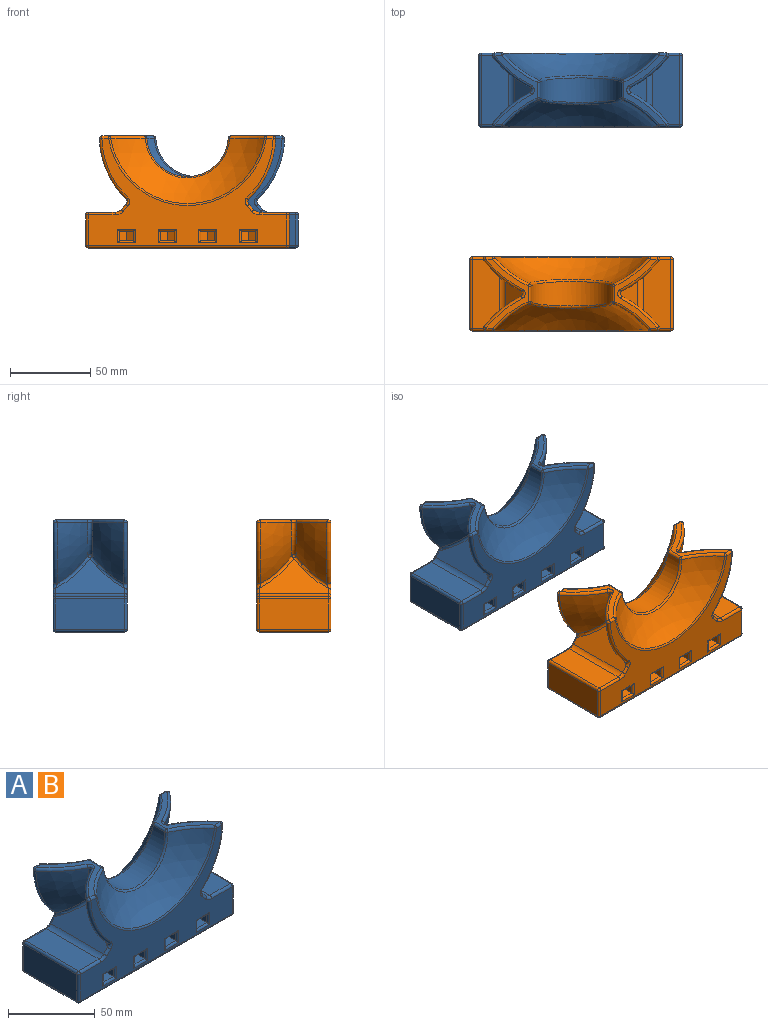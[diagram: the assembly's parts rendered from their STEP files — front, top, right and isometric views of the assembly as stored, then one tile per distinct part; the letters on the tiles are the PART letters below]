
ASSEMBLY  parts=2 mates=2
PART A: 146 faces, bbox 127x74x70.5 mm
  f0: plane 26.9x8.76mm, normal (0,0,-1), area 224.7mm2, adj f85,f98,f99,f100,f138
  f1: plane 26.9x8.76mm, normal (0,0,-1), area 224.7mm2, adj f94,f95,f96,f97,f126
  f2: plane 26.9x8.76mm, normal (0,0,-1), area 224.7mm2, adj f90,f91,f92,f93,f130
  f3: plane 123.83x66.68mm, normal (0,-1,0), area 3245.3mm2, adj f22,f24,f27,f30,f35,f41,f56,f64
  f4: plane 123.83x66.68mm, normal (0,1,0), area 3630mm2, adj f25,f28,f31,f36,f39,f44,f60,f68
  f5: plane 43.05x16.77mm, normal (0,0,1), area 722mm2, adj f20,f74,f76,f77
  f6: plane 43.05x16.77mm, normal (0,0,1), area 722mm2, adj f21,f22,f23,f25
  f7: plane 43.05x26.46mm, normal (0,0,1), area 212.5mm2, adj f52,f53,f55,f56,f57,f58,f60,f61
  f8: plane 43.05x26.46mm, normal (0,0,1), area 212.5mm2, adj f34,f37,f40,f41,f43,f44,f46,f47
  f9: plane 43.05x22.17mm, normal (-0.74,0,0.67), area 649.7mm2, adj f20,f63,f69,f70,f73
  f10: plane 43.05x22.17mm, normal (0.74,0,0.67), area 649.7mm2, adj f21,f26,f27,f31,f32
  f11: sphere r=63.5mm, area 2559.9mm2, adj f46,f51,f57,f82
  f12: sphere r=69.53mm, area 1010.7mm2, adj f61,f62,f68,f69
  f13: sphere r=69.53mm, area 1010.7mm2, adj f32,f33,f39,f40
  f14: sphere r=63.5mm, area 2560mm2, adj f43,f48,f53,f79
  f15: sphere r=69.53mm, area 1010.7mm2, adj f55,f62,f63,f64
  f16: sphere r=69.53mm, area 1010.7mm2, adj f26,f33,f34,f35
  f17: plane 43.05x19.05mm, normal (-1,0,0), area 820.2mm2, adj f76,f111,f117,f118
  f18: plane 43.05x19.05mm, normal (1,0,0), area 820.2mm2, adj f23,f115,f121,f124
  f19: cylinder r=25.4mm len=50.71mm, axis (0,1,0), area 1009.7mm2, adj f47,f48,f51,f52
  f20: cylinder r=5.08mm len=43.05mm, axis (0,-1,0), area 183.2mm2, adj f5,f9,f72,f75
  f21: cylinder r=5.08mm len=43.05mm, axis (0,1,0), area 183.2mm2, adj f6,f10,f24,f28
  f22: cylinder r=1.59mm len=16.77mm, axis (-1,0,0), area 41.8mm2, adj f3,f6,f24,f125
  f23: cylinder r=1.59mm len=43.05mm, axis (0,1,0), area 107.4mm2, adj f6,f18,f112,f125
  f24: torus R=6.67mm, axis (0,1,0), area 11.8mm2, adj f3,f21,f22,f27
  f25: cylinder r=1.59mm len=16.77mm, axis (1,0,0), area 41.8mm2, adj f4,f6,f28,f112
  f26: torus R=71.1mm, axis (0.74,0,0.67), area 77.7mm2, adj f10,f16,f29,f30
  f27: cylinder r=1.59mm len=4.36mm, axis (-0.67,0,0.74), area 11.1mm2, adj f3,f10,f24,f30
  f28: torus R=6.67mm, axis (0,1,0), area 11.8mm2, adj f4,f21,f25,f31
  f29: sphere r=1.59mm, area 4.9mm2, adj f26,f32,f33
  f30: bspline ~5.66x3.15mm, area 11.8mm2, adj f3,f26,f27,f35
  f31: cylinder r=1.59mm len=4.36mm, axis (-0.67,0,0.74), area 11.1mm2, adj f4,f10,f28,f36
  f32: torus R=71.1mm, axis (0.74,0,0.67), area 77.7mm2, adj f10,f13,f29,f36
  f33: torus R=32.03mm, axis (0,1,0), area 79.3mm2, adj f13,f16,f29,f37
  f34: torus R=67.93mm, axis (0,0,1), area 76.4mm2, adj f8,f16,f37,f38
  f35: torus R=53.43mm, axis (0,1,0), area 151.1mm2, adj f3,f16,f30,f38
  f36: bspline ~6.06x3.15mm, area 11.8mm2, adj f4,f31,f32,f39
  f37: bspline ~6.16x2.81mm, area 12.2mm2, adj f8,f33,f34,f40
  f38: sphere r=1.59mm, area 5.8mm2, adj f34,f35,f41
  f39: torus R=53.43mm, axis (0,1,0), area 151.1mm2, adj f4,f13,f36,f42
  f40: torus R=67.93mm, axis (0,0,1), area 76.4mm2, adj f8,f13,f37,f42
  f41: cylinder r=1.59mm len=4.3mm, axis (-1,0,0), area 10.7mm2, adj f3,f8,f38,f78
  f42: sphere r=1.59mm, area 5.8mm2, adj f39,f40,f44
  f43: torus R=64.6mm, axis (0,0,1), area 63.4mm2, adj f8,f14,f45,f78
  f44: cylinder r=1.59mm len=4.3mm, axis (-1,0,0), area 10.7mm2, adj f4,f8,f42,f81
  f45: sphere r=1.59mm, area 2.6mm2, adj f43,f47,f48
  f46: torus R=64.6mm, axis (0,0,1), area 63.4mm2, adj f8,f11,f49,f81
  f47: cylinder r=1.59mm len=9.57mm, axis (0,1,0), area 23mm2, adj f8,f19,f45,f49
  f48: bspline ~52.67x26.83mm, area 132.8mm2, adj f14,f19,f45,f50
  f49: sphere r=1.59mm, area 2.6mm2, adj f46,f47,f51
  f50: sphere r=1.59mm, area 2.6mm2, adj f48,f52,f53
  f51: bspline ~52.67x26.83mm, area 132.8mm2, adj f11,f19,f49,f54
  f52: cylinder r=1.59mm len=9.57mm, axis (0,1,0), area 23mm2, adj f7,f19,f50,f54
  f53: torus R=64.6mm, axis (0,0,1), area 63.4mm2, adj f7,f14,f50,f80
  f54: sphere r=1.59mm, area 2.6mm2, adj f51,f52,f57
  f55: torus R=67.93mm, axis (0,0,1), area 76.4mm2, adj f7,f15,f58,f59
  f56: cylinder r=1.59mm len=4.3mm, axis (-1,0,0), area 10.7mm2, adj f3,f7,f59,f80
  f57: torus R=64.6mm, axis (0,0,1), area 63.4mm2, adj f7,f11,f54,f83
  f58: bspline ~6.16x2.81mm, area 12.2mm2, adj f7,f55,f61,f62
  f59: sphere r=1.59mm, area 5.7mm2, adj f55,f56,f64
  f60: cylinder r=1.59mm len=4.3mm, axis (-1,0,0), area 10.7mm2, adj f4,f7,f65,f83
  f61: torus R=67.93mm, axis (0,0,1), area 76.4mm2, adj f7,f12,f58,f65
  f62: torus R=32.03mm, axis (0,-1,0), area 79.3mm2, adj f12,f15,f58,f66
  f63: torus R=71.1mm, axis (-0.74,0,0.67), area 77.7mm2, adj f9,f15,f66,f67
  f64: torus R=53.43mm, axis (0,1,0), area 151.1mm2, adj f3,f15,f59,f67
  f65: sphere r=1.59mm, area 5.7mm2, adj f60,f61,f68
  f66: sphere r=1.59mm, area 5.3mm2, adj f62,f63,f69
  f67: bspline ~6.06x3.15mm, area 11.8mm2, adj f3,f63,f64,f70
  f68: torus R=53.43mm, axis (0,1,0), area 151.1mm2, adj f4,f12,f65,f71
  f69: torus R=71.1mm, axis (-0.74,0,0.67), area 77.7mm2, adj f9,f12,f66,f71
  f70: cylinder r=1.59mm len=4.36mm, axis (-0.67,0,-0.74), area 11.1mm2, adj f3,f9,f67,f72
  f71: bspline ~5.38x3.15mm, area 11.8mm2, adj f4,f68,f69,f73
  f72: torus R=6.67mm, axis (0,1,0), area 11.8mm2, adj f3,f20,f70,f74
  f73: cylinder r=1.59mm len=4.36mm, axis (-0.67,0,-0.74), area 11.1mm2, adj f4,f9,f71,f75
  f74: cylinder r=1.59mm len=16.77mm, axis (-1,0,0), area 41.8mm2, adj f3,f5,f72,f114
  f75: torus R=6.67mm, axis (0,1,0), area 11.8mm2, adj f4,f20,f73,f77
  f76: cylinder r=1.59mm len=43.05mm, axis (0,-1,0), area 107.4mm2, adj f5,f17,f110,f114
  f77: cylinder r=1.59mm len=16.77mm, axis (1,0,0), area 41.8mm2, adj f4,f5,f75,f110
  f78: sphere r=1.59mm, area 2mm2, adj f41,f43,f79
  f79: torus R=49.75mm, axis (0,1,0), area 191.3mm2, adj f3,f14,f78,f80
  f80: sphere r=1.59mm, area 2mm2, adj f53,f56,f79
  f81: sphere r=1.59mm, area 2mm2, adj f44,f46,f82
  f82: torus R=49.75mm, axis (0,1,0), area 191.3mm2, adj f4,f11,f81,f83
  f83: sphere r=1.59mm, area 2mm2, adj f57,f60,f82
  f84: plane 26.9x8.76mm, normal (0,0,-1), area 224.7mm2, adj f86,f87,f88,f89,f134
  f85: plane 24.37x5.97mm, normal (1,0,0), area 145.5mm2, adj f0,f100,f103,f140
  f86: plane 24.37x5.97mm, normal (-1,0,0), area 145.5mm2, adj f84,f87,f101,f135
  f87: plane 5.97x4.38mm, normal (-0.5,-0.87,0), area 30.2mm2, adj f84,f86,f88,f101
  f88: plane 5.97x4.38mm, normal (0.5,-0.87,0), area 30.2mm2, adj f84,f87,f89,f101
  f89: plane 24.37x5.97mm, normal (1,0,0), area 145.5mm2, adj f84,f88,f101,f136
  f90: plane 24.37x5.97mm, normal (-1,0,0), area 145.5mm2, adj f2,f91,f102,f131
  f91: plane 5.97x4.38mm, normal (-0.5,-0.87,0), area 30.2mm2, adj f2,f90,f92,f102
  f92: plane 5.97x4.38mm, normal (0.5,-0.87,0), area 30.2mm2, adj f2,f91,f93,f102
  f93: plane 24.37x5.97mm, normal (1,0,0), area 145.5mm2, adj f2,f92,f102,f132
  f94: plane 24.37x5.97mm, normal (-1,0,0), area 145.5mm2, adj f1,f95,f109,f127
  f95: plane 5.97x4.38mm, normal (-0.5,-0.87,0), area 30.2mm2, adj f1,f94,f96,f109
  f96: plane 5.97x4.38mm, normal (0.5,-0.87,0), area 30.2mm2, adj f1,f95,f97,f109
  f97: plane 24.37x5.97mm, normal (1,0,0), area 145.5mm2, adj f1,f96,f109,f128
  f98: plane 24.37x5.97mm, normal (-1,0,0), area 145.5mm2, adj f0,f99,f103,f139
  f99: plane 5.97x4.38mm, normal (-0.5,-0.87,0), area 30.2mm2, adj f0,f98,f100,f103
  f100: plane 5.97x4.38mm, normal (0.5,-0.87,0), area 30.2mm2, adj f0,f85,f99,f103
  f101: plane 26.9x8.76mm, normal (0,0,1), area 209.2mm2, adj f86,f87,f88,f89,f107,f137
  f102: plane 26.9x8.76mm, normal (0,0,1), area 209.2mm2, adj f90,f91,f92,f93,f104,f133
  f103: plane 26.9x8.76mm, normal (0,0,1), area 209.2mm2, adj f85,f98,f99,f100,f106,f141
  f104: cylinder r=2.22mm len=4.45mm, axis (0,0,1), area 39.9mm2, adj f102,f145
  f105: cylinder r=2.22mm len=4.45mm, axis (0,0,1), area 39.9mm2, adj f109,f144
  f106: cylinder r=2.22mm len=4.45mm, axis (0,0,1), area 39.9mm2, adj f103,f142
  f107: cylinder r=2.22mm len=4.45mm, axis (0,0,1), area 39.9mm2, adj f101,f143
  f108: plane 123.83x43.05mm, normal (0,0,-1), area 5148.6mm2, adj f116,f117,f121,f122,f142,f143,f144,f145
  f109: plane 26.9x8.76mm, normal (0,0,1), area 209.2mm2, adj f94,f95,f96,f97,f105,f129
  f110: sphere r=1.59mm, area 4mm2, adj f76,f77,f111
  f111: cylinder r=1.59mm len=19.05mm, axis (0,0,-1), area 47.5mm2, adj f4,f17,f110,f113
  f112: sphere r=1.59mm, area 4mm2, adj f23,f25,f115
  f113: sphere r=1.59mm, area 4mm2, adj f111,f116,f117
  f114: sphere r=1.59mm, area 4mm2, adj f74,f76,f118
  f115: cylinder r=1.59mm len=19.05mm, axis (0,0,1), area 47.5mm2, adj f4,f18,f112,f119
  f116: cylinder r=1.59mm len=123.83mm, axis (-1,0,0), area 308.8mm2, adj f4,f108,f113,f119
  f117: cylinder r=1.59mm len=43.05mm, axis (0,1,0), area 107.4mm2, adj f17,f108,f113,f120
  f118: cylinder r=1.59mm len=19.05mm, axis (0,0,1), area 47.5mm2, adj f3,f17,f114,f120
  f119: sphere r=1.59mm, area 4mm2, adj f115,f116,f121
  f120: sphere r=1.59mm, area 4mm2, adj f117,f118,f122
  f121: cylinder r=1.59mm len=43.05mm, axis (0,-1,0), area 107.4mm2, adj f18,f108,f119,f123
  f122: cylinder r=1.59mm len=123.83mm, axis (1,0,0), area 308.8mm2, adj f3,f108,f120,f123
  f123: sphere r=1.59mm, area 4mm2, adj f121,f122,f124
  f124: cylinder r=1.59mm len=19.05mm, axis (0,0,-1), area 47.5mm2, adj f3,f18,f123,f125
  f125: sphere r=1.59mm, area 4mm2, adj f22,f23,f124
  f126: cylinder r=1.27mm len=11.3mm, axis (1,0,0), area 19.3mm2, adj f1,f3,f127,f128
  f127: cylinder r=1.27mm len=8.51mm, axis (0,0,-1), area 13.7mm2, adj f3,f94,f126,f129
  f128: cylinder r=1.27mm len=8.51mm, axis (0,0,1), area 13.7mm2, adj f3,f97,f126,f129
  f129: cylinder r=1.27mm len=11.3mm, axis (-1,0,0), area 19.3mm2, adj f3,f109,f127,f128
  f130: cylinder r=1.27mm len=11.3mm, axis (1,0,0), area 19.3mm2, adj f2,f3,f131,f132
  f131: cylinder r=1.27mm len=8.51mm, axis (0,0,-1), area 13.7mm2, adj f3,f90,f130,f133
  f132: cylinder r=1.27mm len=8.51mm, axis (0,0,1), area 13.7mm2, adj f3,f93,f130,f133
  f133: cylinder r=1.27mm len=11.3mm, axis (-1,0,0), area 19.3mm2, adj f3,f102,f131,f132
  f134: cylinder r=1.27mm len=11.3mm, axis (1,0,0), area 19.3mm2, adj f3,f84,f135,f136
  f135: cylinder r=1.27mm len=8.51mm, axis (0,0,-1), area 13.7mm2, adj f3,f86,f134,f137
  f136: cylinder r=1.27mm len=8.51mm, axis (0,0,1), area 13.7mm2, adj f3,f89,f134,f137
  f137: cylinder r=1.27mm len=11.3mm, axis (-1,0,0), area 19.3mm2, adj f3,f101,f135,f136
  f138: cylinder r=1.27mm len=11.3mm, axis (1,0,0), area 19.3mm2, adj f0,f3,f139,f140
  f139: cylinder r=1.27mm len=8.51mm, axis (0,0,-1), area 13.7mm2, adj f3,f98,f138,f141
  f140: cylinder r=1.27mm len=8.51mm, axis (0,0,1), area 13.7mm2, adj f3,f85,f138,f141
  f141: cylinder r=1.27mm len=11.3mm, axis (-1,0,0), area 19.3mm2, adj f3,f103,f139,f140
  f142: cone r=2.22mm half-angle=45deg, axis (0,0,-1), area 42.5mm2, adj f106,f108
  f143: cone r=2.22mm half-angle=45deg, axis (0,0,-1), area 42.5mm2, adj f107,f108
  f144: cone r=2.22mm half-angle=45deg, axis (0,0,-1), area 42.5mm2, adj f105,f108
  f145: cone r=2.22mm half-angle=45deg, axis (0,0,-1), area 42.5mm2, adj f104,f108
PART B: same geometry as A
PLACE A t=(-104.91,174.03,-125.28)mm
PLACE B t=(-110.54,47.03,-125.28)mm
MATE planar A.f121 <-> B.f121  axis (0,-1,0) through (-43,87.41,-136.39)mm
MATE planar A.f108 <-> B.f108  axis (0,0,-1) through (-104.91,110.53,-137.98)mm
